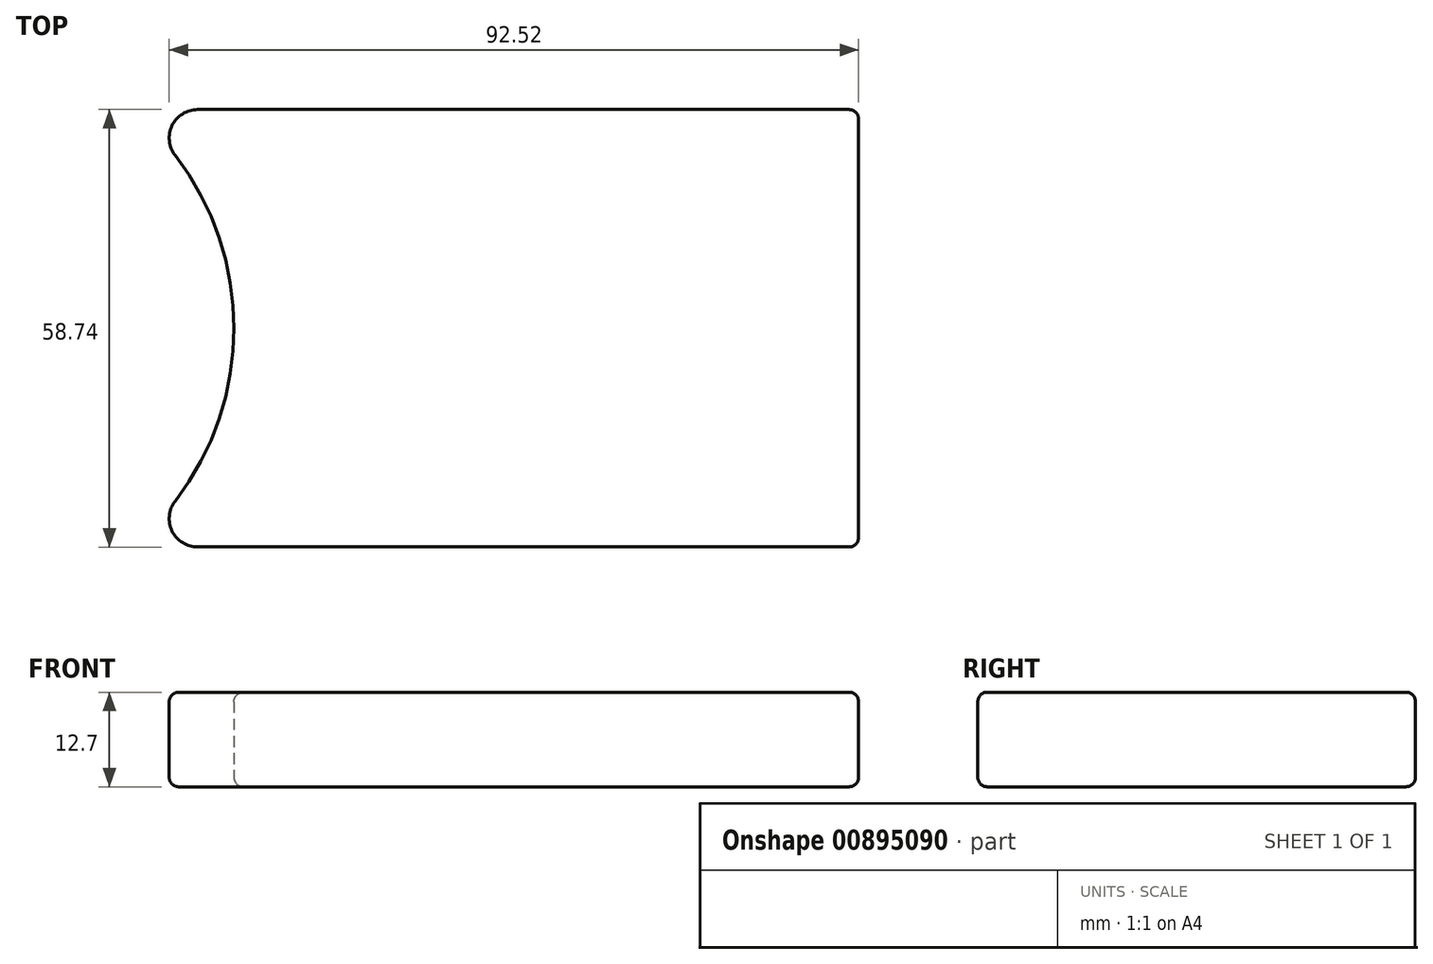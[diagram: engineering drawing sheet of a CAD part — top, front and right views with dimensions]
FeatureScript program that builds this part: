
annotation { "Feature Type Name" : "Feature", "Feature Type Description" : "" }
export const myFeature = defineFeature(function(context is Context, id is Id, definition is map)
    precondition{}
    {
        {
            var Q0;
            Q0=qCreatedBy(makeId("Top.planeOp"),FACE);
            var sketch = newSketch(context, id + "F0", { "sketchPlane" : qUnion([Q0])});
            skLineSegment(sketch, "E0.bottom", {"start": v(-27.35, 29.37) * mm, "end": v(79.18, 29.37) * mm});
            skLineSegment(sketch, "E0.top", {"start": v(-27.35, -29.37) * mm, "end": v(79.18, -29.37) * mm});
            skLineSegment(sketch, "E0.left", {"start": v(-27.35, 29.37) * mm, "end": v(-27.35, -29.37) * mm});
            skLineSegment(sketch, "E0.right", {"start": v(79.18, 29.37) * mm, "end": v(79.18, -29.37) * mm});
            skCircle(sketch, "E1", {"center": v(-42.74, 0) * mm, "radius": 38.1 * mm});
            skPoint(sketch, "E2", {"position": v(-27.35, 0) * mm});
            skSolve(sketch);
        }
        {
            var Q0;
            {var subQ0=sQuery(id+"F0.wireOp",EDGE,"E0.right");Q0=makeQuery(id+"F0.imprint","IMPRINT",FACE,{"disambiguationData":[TD([[makeQuery(id+"F0.imprint","IMPRINT",EDGE,{"derivedFrom":subQ0}),-1.0]])]});}
            extrude(context, id + "F1", {"entities" : qUnion([Q0]), "depth" : 12.7 * mm, "offsetDistance" : 25.4 * mm});
        }
        {
            var Q0;
            Q0=makeQuery(id+"F1.opExtrude","SWEPT_EDGE",EDGE,{"disambiguationData":[OSD([sQuery(id+"F0.wireOp",EDGE,"E0.bottom"),sQuery(id+"F0.wireOp",EDGE,"E1")])]});
            var Q1;
            Q1=makeQuery(id+"F1.opExtrude","SWEPT_EDGE",EDGE,{"disambiguationData":[OSD([sQuery(id+"F0.wireOp",EDGE,"E0.top"),sQuery(id+"F0.wireOp",EDGE,"E1")])]});
            fillet(context, id + "F2", {"entities" : qUnion([Q0, Q1]), "radius" : 3.8 * mm, "tangentPropagation" : true, "allowEdgeOverflow" : false});
        }
        {
            var Q0;
            Q0=makeQuery(id+"F1.opExtrude","CAP_FACE",FACE,{"disambiguationData":[OSD([sQuery(id+"F0.wireOp",EDGE,"E0.bottom"),sQuery(id+"F0.wireOp",EDGE,"E0.top"),sQuery(id+"F0.wireOp",EDGE,"E0.right"),sQuery(id+"F0.wireOp",EDGE,"E1")])],"isStart":false});
            var Q1;
            Q1=makeQuery(id+"F1.opExtrude","CAP_FACE",FACE,{"disambiguationData":[OSD([sQuery(id+"F0.wireOp",EDGE,"E0.bottom"),sQuery(id+"F0.wireOp",EDGE,"E0.top"),sQuery(id+"F0.wireOp",EDGE,"E0.right"),sQuery(id+"F0.wireOp",EDGE,"E1")])],"isStart":true});
            var Q2;
            Q2=makeQuery(id+"F1.opExtrude","SWEPT_FACE",FACE,{"disambiguationData":[OSD([sQuery(id+"F0.wireOp",EDGE,"E0.right")])]});
            fillet(context, id + "F3", {"entities" : qUnion([Q0, Q1, Q2]), "radius" : 1.27 * mm, "tangentPropagation" : true, "allowEdgeOverflow" : false});
        }
    });
